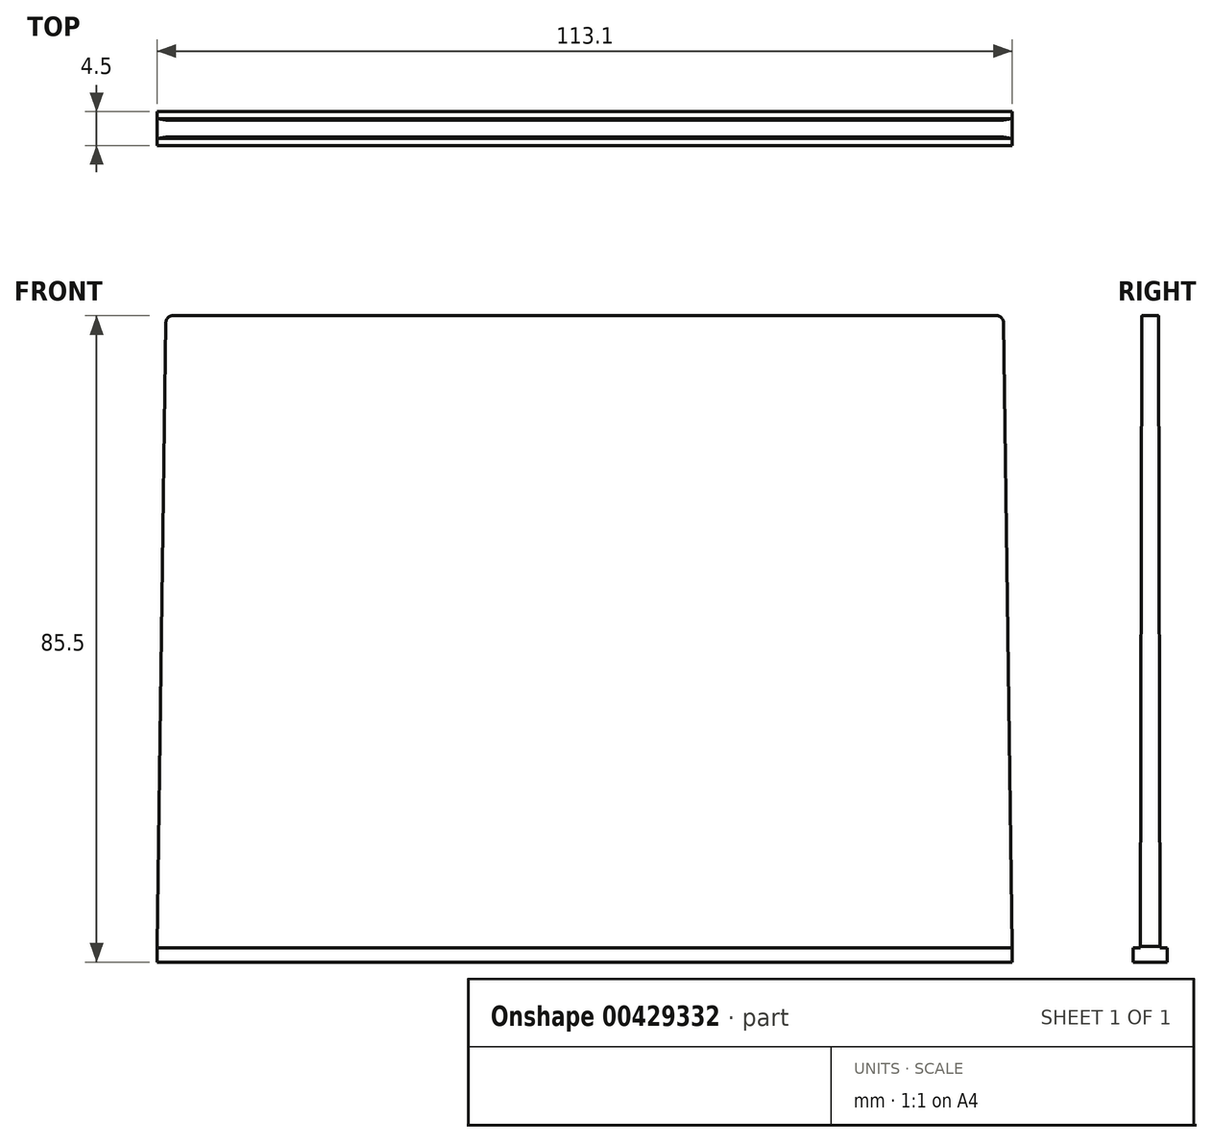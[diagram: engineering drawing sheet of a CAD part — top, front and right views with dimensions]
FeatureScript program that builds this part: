
annotation { "Feature Type Name" : "Feature", "Feature Type Description" : "" }
export const myFeature = defineFeature(function(context is Context, id is Id, definition is map)
    precondition{}
    {
        {
            var Q0;
            Q0=qCreatedBy(makeId("Top.planeOp"),FACE);
            var sketch = newSketch(context, id + "F0", { "sketchPlane" : qUnion([Q0])});
            skLineSegment(sketch, "E0.bottom", {"start": v(-56.55, 2.25) * mm, "end": v(56.55, 2.25) * mm});
            skLineSegment(sketch, "E0.top", {"start": v(-56.55, -2.25) * mm, "end": v(56.55, -2.25) * mm});
            skLineSegment(sketch, "E0.left", {"start": v(-56.55, 2.25) * mm, "end": v(-56.55, -2.25) * mm});
            skLineSegment(sketch, "E0.right", {"start": v(56.55, 2.25) * mm, "end": v(56.55, -2.25) * mm});
            skLineSegment(sketch, "E1", {"start": v(0, 2.25) * mm, "end": v(0, -2.25) * mm});
            skSolve(sketch);
        }
        {
            var Q0;
            {var subQ0=sQuery(id+"F0.wireOp",EDGE,"E0.left");Q0=makeQuery(id+"F0.imprint","IMPRINT",FACE,{"disambiguationData":[TD([[makeQuery(id+"F0.imprint","IMPRINT",EDGE,{"derivedFrom":subQ0}),1.0]])]});}
            var Q1;
            {var subQ0=sQuery(id+"F0.wireOp",EDGE,"E0.right");Q1=makeQuery(id+"F0.imprint","IMPRINT",FACE,{"disambiguationData":[TD([[makeQuery(id+"F0.imprint","IMPRINT",EDGE,{"derivedFrom":subQ0}),-1.0]])]});}
            extrude(context, id + "F1", {"entities" : qUnion([Q0, Q1]), "flatOperationType" : FlatOperationType.REMOVE, "offsetDistance" : 25 * mm, "depth" : 1.9 * mm, "domain" : OperationDomain.MODEL});
        }
        {
            var Q0;
            Q0=makeQuery(id+"F1.opExtrude","CAP_FACE",FACE,{"disambiguationData":[OSD([sQuery(id+"F0.wireOp",EDGE,"E0.bottom"),sQuery(id+"F0.wireOp",EDGE,"E0.top"),sQuery(id+"F0.wireOp",EDGE,"E0.left"),sQuery(id+"F0.wireOp",EDGE,"E0.right")])],"isStart":false});
            var sketch = newSketch(context, id + "F2", { "sketchPlane" : qUnion([Q0])});
            skLineSegment(sketch, "E2.bottom", {"start": v(-55.38, 1.1) * mm, "end": v(55.38, 1.1) * mm});
            skLineSegment(sketch, "E2.top", {"start": v(-55.38, -1.1) * mm, "end": v(55.38, -1.1) * mm});
            skLineSegment(sketch, "E2.left", {"start": v(-55.38, 1.1) * mm, "end": v(-55.38, -1.1) * mm});
            skLineSegment(sketch, "E2.right", {"start": v(55.38, 1.1) * mm, "end": v(55.38, -1.1) * mm});
            skLineSegment(sketch, "E3", {"start": v(0, 1.1) * mm, "end": v(0, -1.1) * mm});
            skSolve(sketch);
        }
        {
            var Q0;
            {var subQ0=sQuery(id+"F2.wireOp",EDGE,"E2.right");Q0=makeQuery(id+"F2.imprint","IMPRINT",FACE,{"disambiguationData":[TD([[makeQuery(id+"F2.imprint","IMPRINT",EDGE,{"derivedFrom":subQ0}),-1.0]])]});}
            var Q1;
            {var subQ0=sQuery(id+"F2.wireOp",EDGE,"E2.left");Q1=makeQuery(id+"F2.imprint","IMPRINT",FACE,{"disambiguationData":[TD([[makeQuery(id+"F2.imprint","IMPRINT",EDGE,{"derivedFrom":subQ0}),1.0]])]});}
            extrude(context, id + "F3", {"entities" : qUnion([Q0, Q1]), "operationType" : NewBodyOperationType.ADD, "flatOperationType" : FlatOperationType.REMOVE, "offsetDistance" : 25 * mm, "depth" : 83.6 * mm, "hasSecondDirection" : true, "secondDirectionOppositeDirection" : false, "secondDirectionDepth" : 83.5 * mm, "domain" : OperationDomain.MODEL});
        }
        {
            var Q0;
            Q0=makeQuery(id+"F1.opExtrude","CAP_FACE",FACE,{"disambiguationData":[OSD([sQuery(id+"F0.wireOp",EDGE,"E0.bottom"),sQuery(id+"F0.wireOp",EDGE,"E0.top"),sQuery(id+"F0.wireOp",EDGE,"E0.left"),sQuery(id+"F0.wireOp",EDGE,"E0.right")])],"isStart":false});
            var sketch = newSketch(context, id + "F4", { "sketchPlane" : qUnion([Q0])});
            skLineSegment(sketch, "E4.bottom", {"start": v(-56.55, 1.32) * mm, "end": v(56.55, 1.32) * mm});
            skLineSegment(sketch, "E4.top", {"start": v(-56.55, -1.32) * mm, "end": v(56.55, -1.32) * mm});
            skLineSegment(sketch, "E4.left", {"start": v(-56.55, 1.32) * mm, "end": v(-56.55, -1.32) * mm});
            skLineSegment(sketch, "E4.right", {"start": v(56.55, 1.32) * mm, "end": v(56.55, -1.32) * mm});
            skLineSegment(sketch, "E5", {"start": v(0, 1.32) * mm, "end": v(0, -1.32) * mm});
            skSolve(sketch);
        }
        {
            var Q0;
            {var subQ0=sQuery(id+"F4.wireOp",EDGE,"E4.right");Q0=makeQuery(id+"F4.imprint","IMPRINT",FACE,{"disambiguationData":[TD([[makeQuery(id+"F4.imprint","IMPRINT",EDGE,{"derivedFrom":subQ0}),-1.0]])]});}
            var Q1;
            {var subQ0=sQuery(id+"F4.wireOp",EDGE,"E4.left");Q1=makeQuery(id+"F4.imprint","IMPRINT",FACE,{"disambiguationData":[TD([[makeQuery(id+"F4.imprint","IMPRINT",EDGE,{"derivedFrom":subQ0}),1.0]])]});}
            extrude(context, id + "F5", {"entities" : qUnion([Q0, Q1]), "operationType" : NewBodyOperationType.ADD, "depth" : 0.2 * mm});
        }
        {
            var Q0;
            Q0=makeQuery(id+"F5.opExtrude","CAP_FACE",FACE,{"disambiguationData":[OSD([sQuery(id+"F4.wireOp",EDGE,"E4.bottom"),sQuery(id+"F4.wireOp",EDGE,"E4.top"),sQuery(id+"F4.wireOp",EDGE,"E4.left"),sQuery(id+"F4.wireOp",EDGE,"E4.right")])],"isStart":false});
            var Q1;
            Q1=makeQuery(id+"F3.opExtrude","CAP_FACE",FACE,{"disambiguationData":[OSD([sQuery(id+"F2.wireOp",EDGE,"E2.bottom"),sQuery(id+"F2.wireOp",EDGE,"E2.top"),sQuery(id+"F2.wireOp",EDGE,"E2.left"),sQuery(id+"F2.wireOp",EDGE,"E2.right")])],"isStart":true});
            loft(context, id + "F6", {"operationType" : NewBodyOperationType.ADD, "sheetProfilesArray" : [{ "sheetProfileEntities" : qUnion([Q0]) }, { "sheetProfileEntities" : qUnion([Q1]) }]});
        }
        {
            var Q0;
            Q0=makeQuery(id+"F5.opExtrude","CAP_EDGE",EDGE,{"disambiguationData":[OSD([sQuery(id+"F4.wireOp",EDGE,"E4.bottom")])],"isStart":true});
            var Q1;
            Q1=makeQuery(id+"F5.opExtrude","CAP_EDGE",EDGE,{"disambiguationData":[OSD([sQuery(id+"F4.wireOp",EDGE,"E4.top")])],"isStart":true});
            var Q2;
            Q2=makeQuery(id+"F3.opExtrude","CAP_EDGE",EDGE,{"disambiguationData":[OSD([sQuery(id+"F2.wireOp",EDGE,"E2.right")])],"isStart":false});
            var Q3;
            Q3=makeQuery(id+"F3.opExtrude","CAP_EDGE",EDGE,{"disambiguationData":[OSD([sQuery(id+"F2.wireOp",EDGE,"E2.left")])],"isStart":false});
            fillet(context, id + "F7", {"entities" : qUnion([Q0, Q1, Q2, Q3]), "radius" : 0.9 * mm, "tangentPropagation" : true, "allowEdgeOverflow" : false});
        }
    });
